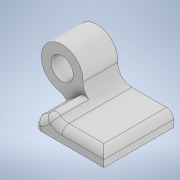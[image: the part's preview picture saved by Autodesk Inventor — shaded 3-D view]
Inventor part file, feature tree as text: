
AUTODESK INVENTOR PART (.ipt)
format: ipt  version: 2021 (Build 250183000, 183)  size: 160,768 bytes
history: native  units: mm
features: fillet x3, extrude x2, sketch x2, projected_geometry x1
ambient origin geometry x8: Origin, YZ Plane, XZ Plane, XY Plane, X Axis, Y Axis, Z Axis, Center Point
bodies: Solid1 (feature_tree)
feature tree (8):
  extrude  "Extrusion1"  Depth=6.0mm
  fillet  "Fillet1"  Radius=1.5mm
  extrude  "Extrusion2"  Depth=10.0mm
  fillet  "Fillet2"  Radius=2.0mm
  fillet  "Fillet3"  Radius=5.0mm
  sketch  "Sketch1"  dims[d0=3.2mm d1=6.0mm d2=1.5mm]
  sketch  "Sketch2"  dims[d3=90.0deg d4=10.0mm d5=2.0mm d6=5.0mm d7=0.0mm d8=2.0mm d9=6.5mm d10=5.0mm d11=0.0mm d12=1.0mm d13=1.0mm]
  projected_geometry  "Projected Loop1"
